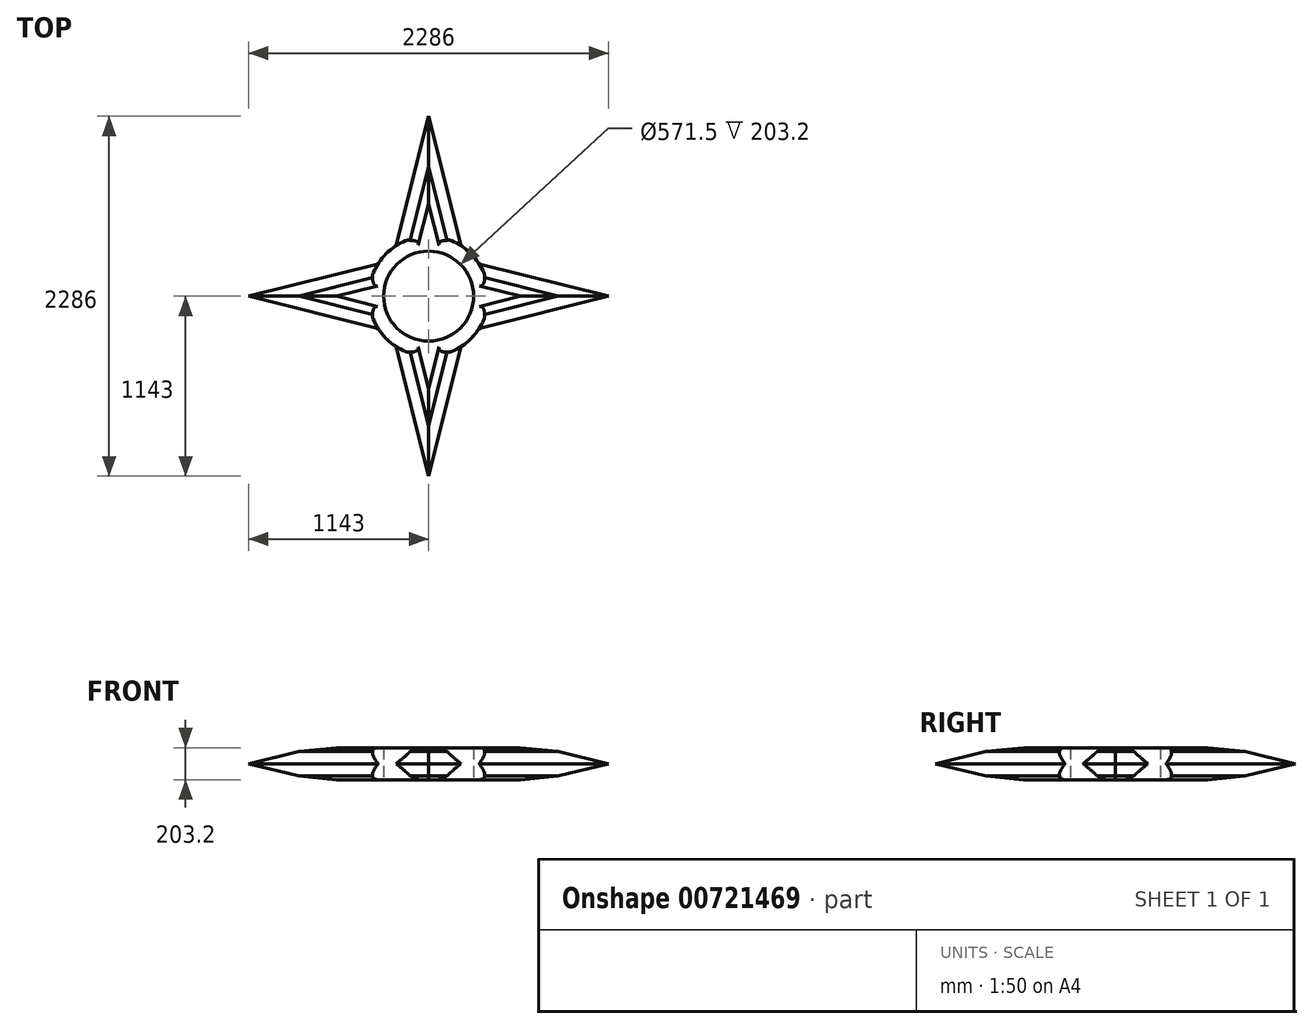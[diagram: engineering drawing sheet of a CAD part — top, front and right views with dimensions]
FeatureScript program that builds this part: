
annotation { "Feature Type Name" : "Feature", "Feature Type Description" : "" }
export const myFeature = defineFeature(function(context is Context, id is Id, definition is map)
    precondition{}
    {
        {
            var Q0;
            Q0=qCreatedBy(makeId("Top.planeOp"),FACE);
            var sketch = newSketch(context, id + "F0", { "sketchPlane" : qUnion([Q0])});
            skCircle(sketch, "E0", {"center": v(0, 0) * mm, "radius": 292.1 * mm});
            skCircle(sketch, "E1", {"center": v(0, 0) * mm, "radius": 381 * mm});
            skLineSegment(sketch, "E2.bottom", {"start": v(0, 0) * mm, "end": v(381, 0) * mm});
            skLineSegment(sketch, "E2.left", {"start": v(0, 0) * mm, "end": v(0, 381) * mm});
            skLineSegment(sketch, "E3.bottom", {"start": v(0, 0) * mm, "end": v(-381, 0) * mm});
            skLineSegment(sketch, "E3.left", {"start": v(0, 0) * mm, "end": v(0, -381) * mm});
            skLineSegment(sketch, "E4", {"start": v(0, 381) * mm, "end": v(0, 1143) * mm});
            skLineSegment(sketch, "E5", {"start": v(381, 0) * mm, "end": v(1143, 0) * mm});
            skLineSegment(sketch, "E6", {"start": v(0, -381) * mm, "end": v(0, -1143) * mm});
            skLineSegment(sketch, "E7", {"start": v(-381, 0) * mm, "end": v(-1143, 0) * mm});
            skLineSegment(sketch, "E8", {"start": v(-190.5, 381) * mm, "end": v(0, 1143) * mm});
            skLineSegment(sketch, "E9", {"start": v(190.5, 381) * mm, "end": v(0, 1143) * mm});
            skLineSegment(sketch, "E10", {"start": v(381, 190.5) * mm, "end": v(1143, 0) * mm});
            skLineSegment(sketch, "E11", {"start": v(1143, 0) * mm, "end": v(381, -190.5) * mm});
            skLineSegment(sketch, "E12", {"start": v(-190.5, -381) * mm, "end": v(0, -1143) * mm});
            skLineSegment(sketch, "E13", {"start": v(190.5, -381) * mm, "end": v(0, -1143) * mm});
            skLineSegment(sketch, "E14", {"start": v(-381, 190.5) * mm, "end": v(-1143, 0) * mm});
            skLineSegment(sketch, "E15", {"start": v(-381, -190.5) * mm, "end": v(-1143, 0) * mm});
            skLineSegment(sketch, "E16", {"start": v(-381, 190.5) * mm, "end": v(-320.8, 205.55) * mm});
            skLineSegment(sketch, "E17", {"start": v(-381, -190.5) * mm, "end": v(-320.8, -205.55) * mm});
            skLineSegment(sketch, "E18", {"start": v(-190.5, 381) * mm, "end": v(-205.55, 320.8) * mm});
            skLineSegment(sketch, "E19", {"start": v(190.5, 381) * mm, "end": v(205.55, 320.8) * mm});
            skLineSegment(sketch, "E20", {"start": v(381, 190.5) * mm, "end": v(320.8, 205.55) * mm});
            skLineSegment(sketch, "E21", {"start": v(381, -190.5) * mm, "end": v(320.8, -205.55) * mm});
            skLineSegment(sketch, "E22", {"start": v(190.5, -381) * mm, "end": v(205.55, -320.8) * mm});
            skLineSegment(sketch, "E23", {"start": v(-190.5, -381) * mm, "end": v(-205.55, -320.8) * mm});
            skCircle(sketch, "E24", {"center": v(0, 0) * mm, "radius": 285.75 * mm});
            skSolve(sketch);
        }
        {
            var Q0;
            {var subQ0=sQuery(id+"F0.wireOp",EDGE,"E4");Q0=makeQuery(id+"F0.imprint","IMPRINT",FACE,{"disambiguationData":[TD([[makeQuery(id+"F0.imprint","IMPRINT",EDGE,{"derivedFrom":subQ0}),1.0]])]});}
            var Q1;
            {var subQ0=sQuery(id+"F0.wireOp",EDGE,"E4");Q1=makeQuery(id+"F0.imprint","IMPRINT",FACE,{"disambiguationData":[TD([[makeQuery(id+"F0.imprint","IMPRINT",EDGE,{"derivedFrom":subQ0}),-1.0]])]});}
            var Q2;
            {var subQ0=sQuery(id+"F0.wireOp",EDGE,"E7");Q2=makeQuery(id+"F0.imprint","IMPRINT",FACE,{"disambiguationData":[TD([[makeQuery(id+"F0.imprint","IMPRINT",EDGE,{"derivedFrom":subQ0}),-1.0]])]});}
            var Q3;
            {var subQ0=sQuery(id+"F0.wireOp",EDGE,"E7");Q3=makeQuery(id+"F0.imprint","IMPRINT",FACE,{"disambiguationData":[TD([[makeQuery(id+"F0.imprint","IMPRINT",EDGE,{"derivedFrom":subQ0}),1.0]])]});}
            var Q4;
            {var subQ0=sQuery(id+"F0.wireOp",EDGE,"E6");Q4=makeQuery(id+"F0.imprint","IMPRINT",FACE,{"disambiguationData":[TD([[makeQuery(id+"F0.imprint","IMPRINT",EDGE,{"derivedFrom":subQ0}),-1.0]])]});}
            var Q5;
            {var subQ0=sQuery(id+"F0.wireOp",EDGE,"E6");Q5=makeQuery(id+"F0.imprint","IMPRINT",FACE,{"disambiguationData":[TD([[makeQuery(id+"F0.imprint","IMPRINT",EDGE,{"derivedFrom":subQ0}),1.0]])]});}
            var Q6;
            {var subQ0=sQuery(id+"F0.wireOp",EDGE,"E5");Q6=makeQuery(id+"F0.imprint","IMPRINT",FACE,{"disambiguationData":[TD([[makeQuery(id+"F0.imprint","IMPRINT",EDGE,{"derivedFrom":subQ0}),-1.0]])]});}
            var Q7;
            {var subQ0=sQuery(id+"F0.wireOp",EDGE,"E5");Q7=makeQuery(id+"F0.imprint","IMPRINT",FACE,{"disambiguationData":[TD([[makeQuery(id+"F0.imprint","IMPRINT",EDGE,{"derivedFrom":subQ0}),1.0]])]});}
            var Q8;
            {var subQ0=sQuery(id+"F0.wireOp",EDGE,"E2.left");var subQ6=sQuery(id+"F0.wireOp",EDGE,"E0");var subQ9=makeQuery(id+"F0.imprint","INTERSECT",VERTEX,{"derivedFrom":[subQ6,subQ0]});Q8=makeQuery(id+"F0.imprint","IMPRINT",FACE,{"disambiguationData":[TD([[makeQuery(id+"F0.imprint","IMPRINT",EDGE,{"disambiguationData":[TD([[subQ9,1.0]])],"derivedFrom":subQ6}),-1.0]])]});}
            var Q9;
            {var subQ5=sQuery(id+"F0.wireOp",EDGE,"E2.left");var subQ7=sQuery(id+"F0.wireOp",EDGE,"E0");var subQ8=makeQuery(id+"F0.imprint","INTERSECT",VERTEX,{"derivedFrom":[subQ7,subQ5]});Q9=makeQuery(id+"F0.imprint","IMPRINT",FACE,{"disambiguationData":[TD([[makeQuery(id+"F0.imprint","IMPRINT",EDGE,{"disambiguationData":[TD([[subQ8,-1.0]])],"derivedFrom":subQ7}),-1.0]])]});}
            var Q10;
            {var subQ0=sQuery(id+"F0.wireOp",EDGE,"E2.bottom");var subQ5=sQuery(id+"F0.wireOp",EDGE,"E0");var subQ6=makeQuery(id+"F0.imprint","INTERSECT",VERTEX,{"derivedFrom":[subQ5,subQ0]});Q10=makeQuery(id+"F0.imprint","IMPRINT",FACE,{"disambiguationData":[TD([[makeQuery(id+"F0.imprint","IMPRINT",EDGE,{"disambiguationData":[TD([[subQ6,1.0]])],"derivedFrom":subQ5}),-1.0]])]});}
            var Q11;
            {var subQ0=sQuery(id+"F0.wireOp",EDGE,"E3.bottom");var subQ1=sQuery(id+"F0.wireOp",EDGE,"E0");var subQ2=makeQuery(id+"F0.imprint","INTERSECT",VERTEX,{"derivedFrom":[subQ1,subQ0]});Q11=makeQuery(id+"F0.imprint","IMPRINT",FACE,{"disambiguationData":[TD([[makeQuery(id+"F0.imprint","IMPRINT",EDGE,{"disambiguationData":[TD([[subQ2,-1.0]])],"derivedFrom":subQ1}),1.0]])]});}
            var Q12;
            {var subQ0=sQuery(id+"F0.wireOp",EDGE,"E2.left");var subQ1=sQuery(id+"F0.wireOp",EDGE,"E0");var subQ2=makeQuery(id+"F0.imprint","INTERSECT",VERTEX,{"derivedFrom":[subQ1,subQ0]});Q12=makeQuery(id+"F0.imprint","IMPRINT",FACE,{"disambiguationData":[TD([[makeQuery(id+"F0.imprint","IMPRINT",EDGE,{"disambiguationData":[TD([[subQ2,-1.0]])],"derivedFrom":subQ1}),1.0]])]});}
            var Q13;
            {var subQ0=sQuery(id+"F0.wireOp",EDGE,"E2.bottom");var subQ1=sQuery(id+"F0.wireOp",EDGE,"E0");var subQ2=makeQuery(id+"F0.imprint","INTERSECT",VERTEX,{"derivedFrom":[subQ1,subQ0]});Q13=makeQuery(id+"F0.imprint","IMPRINT",FACE,{"disambiguationData":[TD([[makeQuery(id+"F0.imprint","IMPRINT",EDGE,{"disambiguationData":[TD([[subQ2,1.0]])],"derivedFrom":subQ1}),1.0]])]});}
            var Q14;
            {var subQ0=sQuery(id+"F0.wireOp",EDGE,"E2.left");var subQ1=sQuery(id+"F0.wireOp",EDGE,"E0");var subQ2=makeQuery(id+"F0.imprint","INTERSECT",VERTEX,{"derivedFrom":[subQ1,subQ0]});Q14=makeQuery(id+"F0.imprint","IMPRINT",FACE,{"disambiguationData":[TD([[makeQuery(id+"F0.imprint","IMPRINT",EDGE,{"disambiguationData":[TD([[subQ2,1.0]])],"derivedFrom":subQ1}),1.0]])]});}
            var Q15;
            {var subQ3=sQuery(id+"F0.wireOp",EDGE,"E3.bottom");var subQ7=sQuery(id+"F0.wireOp",EDGE,"E0");var subQ8=makeQuery(id+"F0.imprint","INTERSECT",VERTEX,{"derivedFrom":[subQ7,subQ3]});Q15=makeQuery(id+"F0.imprint","IMPRINT",FACE,{"disambiguationData":[TD([[makeQuery(id+"F0.imprint","IMPRINT",EDGE,{"disambiguationData":[TD([[subQ8,-1.0]])],"derivedFrom":subQ7}),-1.0]])]});}
            extrude(context, id + "F1", {"entities" : qUnion([Q0, Q1, Q2, Q3, Q4, Q5, Q6, Q7, Q8, Q9, Q10, Q11, Q12, Q13, Q14, Q15]), "depth" : 203.2 * mm, "offsetDistance" : 25.4 * mm});
        }
        {
            var Q0;
            Q0=makeQuery(id+"F1.opExtrude","CAP_EDGE",EDGE,{"disambiguationData":[OSD([sQuery(id+"F0.wireOp",EDGE,"E15"),sQuery(id+"F0.wireOp",EDGE,"E17")])],"isStart":false});
            var Q1;
            Q1=makeQuery(id+"F1.opExtrude","CAP_EDGE",EDGE,{"disambiguationData":[OSD([sQuery(id+"F0.wireOp",EDGE,"E15"),sQuery(id+"F0.wireOp",EDGE,"E17")])],"isStart":true});
            var Q2;
            Q2=makeQuery(id+"F1.opExtrude","CAP_EDGE",EDGE,{"disambiguationData":[OSD([sQuery(id+"F0.wireOp",EDGE,"E14"),sQuery(id+"F0.wireOp",EDGE,"E16")])],"isStart":false});
            var Q3;
            Q3=makeQuery(id+"F1.opExtrude","CAP_EDGE",EDGE,{"disambiguationData":[OSD([sQuery(id+"F0.wireOp",EDGE,"E14"),sQuery(id+"F0.wireOp",EDGE,"E16")])],"isStart":true});
            var Q4;
            Q4=makeQuery(id+"F1.opExtrude","CAP_EDGE",EDGE,{"disambiguationData":[OSD([sQuery(id+"F0.wireOp",EDGE,"E8"),sQuery(id+"F0.wireOp",EDGE,"E18")])],"isStart":false});
            var Q5;
            Q5=makeQuery(id+"F1.opExtrude","CAP_EDGE",EDGE,{"disambiguationData":[OSD([sQuery(id+"F0.wireOp",EDGE,"E8"),sQuery(id+"F0.wireOp",EDGE,"E18")])],"isStart":true});
            var Q6;
            Q6=makeQuery(id+"F1.opExtrude","CAP_EDGE",EDGE,{"disambiguationData":[OSD([sQuery(id+"F0.wireOp",EDGE,"E9"),sQuery(id+"F0.wireOp",EDGE,"E19")])],"isStart":false});
            var Q7;
            Q7=makeQuery(id+"F1.opExtrude","CAP_EDGE",EDGE,{"disambiguationData":[OSD([sQuery(id+"F0.wireOp",EDGE,"E9"),sQuery(id+"F0.wireOp",EDGE,"E19")])],"isStart":true});
            var Q8;
            Q8=makeQuery(id+"F1.opExtrude","CAP_EDGE",EDGE,{"disambiguationData":[OSD([sQuery(id+"F0.wireOp",EDGE,"E10"),sQuery(id+"F0.wireOp",EDGE,"E20")])],"isStart":false});
            var Q9;
            Q9=makeQuery(id+"F1.opExtrude","CAP_EDGE",EDGE,{"disambiguationData":[OSD([sQuery(id+"F0.wireOp",EDGE,"E10"),sQuery(id+"F0.wireOp",EDGE,"E20")])],"isStart":true});
            var Q10;
            Q10=makeQuery(id+"F1.opExtrude","CAP_EDGE",EDGE,{"disambiguationData":[OSD([sQuery(id+"F0.wireOp",EDGE,"E11"),sQuery(id+"F0.wireOp",EDGE,"E21")])],"isStart":false});
            var Q11;
            Q11=makeQuery(id+"F1.opExtrude","CAP_EDGE",EDGE,{"disambiguationData":[OSD([sQuery(id+"F0.wireOp",EDGE,"E11"),sQuery(id+"F0.wireOp",EDGE,"E21")])],"isStart":true});
            var Q12;
            Q12=makeQuery(id+"F1.opExtrude","CAP_EDGE",EDGE,{"disambiguationData":[OSD([sQuery(id+"F0.wireOp",EDGE,"E13"),sQuery(id+"F0.wireOp",EDGE,"E22")])],"isStart":false});
            var Q13;
            Q13=makeQuery(id+"F1.opExtrude","CAP_EDGE",EDGE,{"disambiguationData":[OSD([sQuery(id+"F0.wireOp",EDGE,"E13"),sQuery(id+"F0.wireOp",EDGE,"E22")])],"isStart":true});
            var Q14;
            Q14=makeQuery(id+"F1.opExtrude","CAP_EDGE",EDGE,{"disambiguationData":[OSD([sQuery(id+"F0.wireOp",EDGE,"E12"),sQuery(id+"F0.wireOp",EDGE,"E23")])],"isStart":false});
            var Q15;
            Q15=makeQuery(id+"F1.opExtrude","CAP_EDGE",EDGE,{"disambiguationData":[OSD([sQuery(id+"F0.wireOp",EDGE,"E12"),sQuery(id+"F0.wireOp",EDGE,"E23")])],"isStart":true});
            chamfer(context, id + "F2", {"entities" : qUnion([Q0, Q1, Q2, Q3, Q4, Q5, Q6, Q7, Q8, Q9, Q10, Q11, Q12, Q13, Q14, Q15]), "width" : 101.6 * mm, "tangentPropagation" : true});
        }
        {
            var Q0;
            {var subQ0=sQuery(id+"F0.wireOp",EDGE,"E23");var subQ1=sQuery(id+"F0.wireOp",EDGE,"E12");Q0=makeQuery(id+"F2.opChamfer","BLEND_EDGE",EDGE,{"blendedFrom":[makeQuery(id+"F1.opExtrude","CAP_EDGE",EDGE,{"disambiguationData":[OSD([subQ1,subQ0])],"isStart":false}),makeQuery(id+"F1.opExtrude","CAP_FACE",FACE,{"disambiguationData":[OSD([sQuery(id+"F0.wireOp",EDGE,"E0"),sQuery(id+"F0.wireOp",EDGE,"E1"),sQuery(id+"F0.wireOp",EDGE,"E8"),sQuery(id+"F0.wireOp",EDGE,"E9"),sQuery(id+"F0.wireOp",EDGE,"E10"),sQuery(id+"F0.wireOp",EDGE,"E11"),subQ1,sQuery(id+"F0.wireOp",EDGE,"E13"),sQuery(id+"F0.wireOp",EDGE,"E14"),sQuery(id+"F0.wireOp",EDGE,"E15"),sQuery(id+"F0.wireOp",EDGE,"E16"),sQuery(id+"F0.wireOp",EDGE,"E17"),sQuery(id+"F0.wireOp",EDGE,"E18"),sQuery(id+"F0.wireOp",EDGE,"E19"),sQuery(id+"F0.wireOp",EDGE,"E20"),sQuery(id+"F0.wireOp",EDGE,"E21"),sQuery(id+"F0.wireOp",EDGE,"E22"),subQ0])],"isStart":false})],"blendedInto":[makeQuery(id+"F1.opExtrude","CAP_FACE",FACE,{"disambiguationData":[OSD([sQuery(id+"F0.wireOp",EDGE,"E0"),sQuery(id+"F0.wireOp",EDGE,"E1"),sQuery(id+"F0.wireOp",EDGE,"E8"),sQuery(id+"F0.wireOp",EDGE,"E9"),sQuery(id+"F0.wireOp",EDGE,"E10"),sQuery(id+"F0.wireOp",EDGE,"E11"),subQ1,sQuery(id+"F0.wireOp",EDGE,"E13"),sQuery(id+"F0.wireOp",EDGE,"E14"),sQuery(id+"F0.wireOp",EDGE,"E15"),sQuery(id+"F0.wireOp",EDGE,"E16"),sQuery(id+"F0.wireOp",EDGE,"E17"),sQuery(id+"F0.wireOp",EDGE,"E18"),sQuery(id+"F0.wireOp",EDGE,"E19"),sQuery(id+"F0.wireOp",EDGE,"E20"),sQuery(id+"F0.wireOp",EDGE,"E21"),sQuery(id+"F0.wireOp",EDGE,"E22"),subQ0])],"isStart":false})]});}
            var Q1;
            {var subQ0=sQuery(id+"F0.wireOp",EDGE,"E22");var subQ1=sQuery(id+"F0.wireOp",EDGE,"E13");Q1=makeQuery(id+"F2.opChamfer","BLEND_EDGE",EDGE,{"blendedFrom":[makeQuery(id+"F1.opExtrude","CAP_EDGE",EDGE,{"disambiguationData":[OSD([subQ1,subQ0])],"isStart":false}),makeQuery(id+"F1.opExtrude","CAP_FACE",FACE,{"disambiguationData":[OSD([sQuery(id+"F0.wireOp",EDGE,"E0"),sQuery(id+"F0.wireOp",EDGE,"E1"),sQuery(id+"F0.wireOp",EDGE,"E8"),sQuery(id+"F0.wireOp",EDGE,"E9"),sQuery(id+"F0.wireOp",EDGE,"E10"),sQuery(id+"F0.wireOp",EDGE,"E11"),sQuery(id+"F0.wireOp",EDGE,"E12"),subQ1,sQuery(id+"F0.wireOp",EDGE,"E14"),sQuery(id+"F0.wireOp",EDGE,"E15"),sQuery(id+"F0.wireOp",EDGE,"E16"),sQuery(id+"F0.wireOp",EDGE,"E17"),sQuery(id+"F0.wireOp",EDGE,"E18"),sQuery(id+"F0.wireOp",EDGE,"E19"),sQuery(id+"F0.wireOp",EDGE,"E20"),sQuery(id+"F0.wireOp",EDGE,"E21"),subQ0,sQuery(id+"F0.wireOp",EDGE,"E23")])],"isStart":false})],"blendedInto":[makeQuery(id+"F1.opExtrude","CAP_FACE",FACE,{"disambiguationData":[OSD([sQuery(id+"F0.wireOp",EDGE,"E0"),sQuery(id+"F0.wireOp",EDGE,"E1"),sQuery(id+"F0.wireOp",EDGE,"E8"),sQuery(id+"F0.wireOp",EDGE,"E9"),sQuery(id+"F0.wireOp",EDGE,"E10"),sQuery(id+"F0.wireOp",EDGE,"E11"),sQuery(id+"F0.wireOp",EDGE,"E12"),subQ1,sQuery(id+"F0.wireOp",EDGE,"E14"),sQuery(id+"F0.wireOp",EDGE,"E15"),sQuery(id+"F0.wireOp",EDGE,"E16"),sQuery(id+"F0.wireOp",EDGE,"E17"),sQuery(id+"F0.wireOp",EDGE,"E18"),sQuery(id+"F0.wireOp",EDGE,"E19"),sQuery(id+"F0.wireOp",EDGE,"E20"),sQuery(id+"F0.wireOp",EDGE,"E21"),subQ0,sQuery(id+"F0.wireOp",EDGE,"E23")])],"isStart":false})]});}
            var Q2;
            {var subQ0=sQuery(id+"F0.wireOp",EDGE,"E21");var subQ1=sQuery(id+"F0.wireOp",EDGE,"E11");Q2=makeQuery(id+"F2.opChamfer","BLEND_EDGE",EDGE,{"blendedFrom":[makeQuery(id+"F1.opExtrude","CAP_EDGE",EDGE,{"disambiguationData":[OSD([subQ1,subQ0])],"isStart":false}),makeQuery(id+"F1.opExtrude","CAP_FACE",FACE,{"disambiguationData":[OSD([sQuery(id+"F0.wireOp",EDGE,"E0"),sQuery(id+"F0.wireOp",EDGE,"E1"),sQuery(id+"F0.wireOp",EDGE,"E8"),sQuery(id+"F0.wireOp",EDGE,"E9"),sQuery(id+"F0.wireOp",EDGE,"E10"),subQ1,sQuery(id+"F0.wireOp",EDGE,"E12"),sQuery(id+"F0.wireOp",EDGE,"E13"),sQuery(id+"F0.wireOp",EDGE,"E14"),sQuery(id+"F0.wireOp",EDGE,"E15"),sQuery(id+"F0.wireOp",EDGE,"E16"),sQuery(id+"F0.wireOp",EDGE,"E17"),sQuery(id+"F0.wireOp",EDGE,"E18"),sQuery(id+"F0.wireOp",EDGE,"E19"),sQuery(id+"F0.wireOp",EDGE,"E20"),subQ0,sQuery(id+"F0.wireOp",EDGE,"E22"),sQuery(id+"F0.wireOp",EDGE,"E23")])],"isStart":false})],"blendedInto":[makeQuery(id+"F1.opExtrude","CAP_FACE",FACE,{"disambiguationData":[OSD([sQuery(id+"F0.wireOp",EDGE,"E0"),sQuery(id+"F0.wireOp",EDGE,"E1"),sQuery(id+"F0.wireOp",EDGE,"E8"),sQuery(id+"F0.wireOp",EDGE,"E9"),sQuery(id+"F0.wireOp",EDGE,"E10"),subQ1,sQuery(id+"F0.wireOp",EDGE,"E12"),sQuery(id+"F0.wireOp",EDGE,"E13"),sQuery(id+"F0.wireOp",EDGE,"E14"),sQuery(id+"F0.wireOp",EDGE,"E15"),sQuery(id+"F0.wireOp",EDGE,"E16"),sQuery(id+"F0.wireOp",EDGE,"E17"),sQuery(id+"F0.wireOp",EDGE,"E18"),sQuery(id+"F0.wireOp",EDGE,"E19"),sQuery(id+"F0.wireOp",EDGE,"E20"),subQ0,sQuery(id+"F0.wireOp",EDGE,"E22"),sQuery(id+"F0.wireOp",EDGE,"E23")])],"isStart":false})]});}
            var Q3;
            {var subQ0=sQuery(id+"F0.wireOp",EDGE,"E20");var subQ1=sQuery(id+"F0.wireOp",EDGE,"E10");Q3=makeQuery(id+"F2.opChamfer","BLEND_EDGE",EDGE,{"blendedFrom":[makeQuery(id+"F1.opExtrude","CAP_EDGE",EDGE,{"disambiguationData":[OSD([subQ1,subQ0])],"isStart":false}),makeQuery(id+"F1.opExtrude","CAP_FACE",FACE,{"disambiguationData":[OSD([sQuery(id+"F0.wireOp",EDGE,"E0"),sQuery(id+"F0.wireOp",EDGE,"E1"),sQuery(id+"F0.wireOp",EDGE,"E8"),sQuery(id+"F0.wireOp",EDGE,"E9"),subQ1,sQuery(id+"F0.wireOp",EDGE,"E11"),sQuery(id+"F0.wireOp",EDGE,"E12"),sQuery(id+"F0.wireOp",EDGE,"E13"),sQuery(id+"F0.wireOp",EDGE,"E14"),sQuery(id+"F0.wireOp",EDGE,"E15"),sQuery(id+"F0.wireOp",EDGE,"E16"),sQuery(id+"F0.wireOp",EDGE,"E17"),sQuery(id+"F0.wireOp",EDGE,"E18"),sQuery(id+"F0.wireOp",EDGE,"E19"),subQ0,sQuery(id+"F0.wireOp",EDGE,"E21"),sQuery(id+"F0.wireOp",EDGE,"E22"),sQuery(id+"F0.wireOp",EDGE,"E23")])],"isStart":false})],"blendedInto":[makeQuery(id+"F1.opExtrude","CAP_FACE",FACE,{"disambiguationData":[OSD([sQuery(id+"F0.wireOp",EDGE,"E0"),sQuery(id+"F0.wireOp",EDGE,"E1"),sQuery(id+"F0.wireOp",EDGE,"E8"),sQuery(id+"F0.wireOp",EDGE,"E9"),subQ1,sQuery(id+"F0.wireOp",EDGE,"E11"),sQuery(id+"F0.wireOp",EDGE,"E12"),sQuery(id+"F0.wireOp",EDGE,"E13"),sQuery(id+"F0.wireOp",EDGE,"E14"),sQuery(id+"F0.wireOp",EDGE,"E15"),sQuery(id+"F0.wireOp",EDGE,"E16"),sQuery(id+"F0.wireOp",EDGE,"E17"),sQuery(id+"F0.wireOp",EDGE,"E18"),sQuery(id+"F0.wireOp",EDGE,"E19"),subQ0,sQuery(id+"F0.wireOp",EDGE,"E21"),sQuery(id+"F0.wireOp",EDGE,"E22"),sQuery(id+"F0.wireOp",EDGE,"E23")])],"isStart":false})]});}
            var Q4;
            {var subQ0=sQuery(id+"F0.wireOp",EDGE,"E19");var subQ1=sQuery(id+"F0.wireOp",EDGE,"E9");Q4=makeQuery(id+"F2.opChamfer","BLEND_EDGE",EDGE,{"blendedFrom":[makeQuery(id+"F1.opExtrude","CAP_EDGE",EDGE,{"disambiguationData":[OSD([subQ1,subQ0])],"isStart":false}),makeQuery(id+"F1.opExtrude","CAP_FACE",FACE,{"disambiguationData":[OSD([sQuery(id+"F0.wireOp",EDGE,"E0"),sQuery(id+"F0.wireOp",EDGE,"E1"),sQuery(id+"F0.wireOp",EDGE,"E8"),subQ1,sQuery(id+"F0.wireOp",EDGE,"E10"),sQuery(id+"F0.wireOp",EDGE,"E11"),sQuery(id+"F0.wireOp",EDGE,"E12"),sQuery(id+"F0.wireOp",EDGE,"E13"),sQuery(id+"F0.wireOp",EDGE,"E14"),sQuery(id+"F0.wireOp",EDGE,"E15"),sQuery(id+"F0.wireOp",EDGE,"E16"),sQuery(id+"F0.wireOp",EDGE,"E17"),sQuery(id+"F0.wireOp",EDGE,"E18"),subQ0,sQuery(id+"F0.wireOp",EDGE,"E20"),sQuery(id+"F0.wireOp",EDGE,"E21"),sQuery(id+"F0.wireOp",EDGE,"E22"),sQuery(id+"F0.wireOp",EDGE,"E23")])],"isStart":false})],"blendedInto":[makeQuery(id+"F1.opExtrude","CAP_FACE",FACE,{"disambiguationData":[OSD([sQuery(id+"F0.wireOp",EDGE,"E0"),sQuery(id+"F0.wireOp",EDGE,"E1"),sQuery(id+"F0.wireOp",EDGE,"E8"),subQ1,sQuery(id+"F0.wireOp",EDGE,"E10"),sQuery(id+"F0.wireOp",EDGE,"E11"),sQuery(id+"F0.wireOp",EDGE,"E12"),sQuery(id+"F0.wireOp",EDGE,"E13"),sQuery(id+"F0.wireOp",EDGE,"E14"),sQuery(id+"F0.wireOp",EDGE,"E15"),sQuery(id+"F0.wireOp",EDGE,"E16"),sQuery(id+"F0.wireOp",EDGE,"E17"),sQuery(id+"F0.wireOp",EDGE,"E18"),subQ0,sQuery(id+"F0.wireOp",EDGE,"E20"),sQuery(id+"F0.wireOp",EDGE,"E21"),sQuery(id+"F0.wireOp",EDGE,"E22"),sQuery(id+"F0.wireOp",EDGE,"E23")])],"isStart":false})]});}
            var Q5;
            {var subQ0=sQuery(id+"F0.wireOp",EDGE,"E18");var subQ1=sQuery(id+"F0.wireOp",EDGE,"E8");Q5=makeQuery(id+"F2.opChamfer","BLEND_EDGE",EDGE,{"blendedFrom":[makeQuery(id+"F1.opExtrude","CAP_EDGE",EDGE,{"disambiguationData":[OSD([subQ1,subQ0])],"isStart":false}),makeQuery(id+"F1.opExtrude","CAP_FACE",FACE,{"disambiguationData":[OSD([sQuery(id+"F0.wireOp",EDGE,"E0"),sQuery(id+"F0.wireOp",EDGE,"E1"),subQ1,sQuery(id+"F0.wireOp",EDGE,"E9"),sQuery(id+"F0.wireOp",EDGE,"E10"),sQuery(id+"F0.wireOp",EDGE,"E11"),sQuery(id+"F0.wireOp",EDGE,"E12"),sQuery(id+"F0.wireOp",EDGE,"E13"),sQuery(id+"F0.wireOp",EDGE,"E14"),sQuery(id+"F0.wireOp",EDGE,"E15"),sQuery(id+"F0.wireOp",EDGE,"E16"),sQuery(id+"F0.wireOp",EDGE,"E17"),subQ0,sQuery(id+"F0.wireOp",EDGE,"E19"),sQuery(id+"F0.wireOp",EDGE,"E20"),sQuery(id+"F0.wireOp",EDGE,"E21"),sQuery(id+"F0.wireOp",EDGE,"E22"),sQuery(id+"F0.wireOp",EDGE,"E23")])],"isStart":false})],"blendedInto":[makeQuery(id+"F1.opExtrude","CAP_FACE",FACE,{"disambiguationData":[OSD([sQuery(id+"F0.wireOp",EDGE,"E0"),sQuery(id+"F0.wireOp",EDGE,"E1"),subQ1,sQuery(id+"F0.wireOp",EDGE,"E9"),sQuery(id+"F0.wireOp",EDGE,"E10"),sQuery(id+"F0.wireOp",EDGE,"E11"),sQuery(id+"F0.wireOp",EDGE,"E12"),sQuery(id+"F0.wireOp",EDGE,"E13"),sQuery(id+"F0.wireOp",EDGE,"E14"),sQuery(id+"F0.wireOp",EDGE,"E15"),sQuery(id+"F0.wireOp",EDGE,"E16"),sQuery(id+"F0.wireOp",EDGE,"E17"),subQ0,sQuery(id+"F0.wireOp",EDGE,"E19"),sQuery(id+"F0.wireOp",EDGE,"E20"),sQuery(id+"F0.wireOp",EDGE,"E21"),sQuery(id+"F0.wireOp",EDGE,"E22"),sQuery(id+"F0.wireOp",EDGE,"E23")])],"isStart":false})]});}
            var Q6;
            {var subQ0=sQuery(id+"F0.wireOp",EDGE,"E16");var subQ1=sQuery(id+"F0.wireOp",EDGE,"E14");Q6=makeQuery(id+"F2.opChamfer","BLEND_EDGE",EDGE,{"blendedFrom":[makeQuery(id+"F1.opExtrude","CAP_EDGE",EDGE,{"disambiguationData":[OSD([subQ1,subQ0])],"isStart":false}),makeQuery(id+"F1.opExtrude","CAP_FACE",FACE,{"disambiguationData":[OSD([sQuery(id+"F0.wireOp",EDGE,"E0"),sQuery(id+"F0.wireOp",EDGE,"E1"),sQuery(id+"F0.wireOp",EDGE,"E8"),sQuery(id+"F0.wireOp",EDGE,"E9"),sQuery(id+"F0.wireOp",EDGE,"E10"),sQuery(id+"F0.wireOp",EDGE,"E11"),sQuery(id+"F0.wireOp",EDGE,"E12"),sQuery(id+"F0.wireOp",EDGE,"E13"),subQ1,sQuery(id+"F0.wireOp",EDGE,"E15"),subQ0,sQuery(id+"F0.wireOp",EDGE,"E17"),sQuery(id+"F0.wireOp",EDGE,"E18"),sQuery(id+"F0.wireOp",EDGE,"E19"),sQuery(id+"F0.wireOp",EDGE,"E20"),sQuery(id+"F0.wireOp",EDGE,"E21"),sQuery(id+"F0.wireOp",EDGE,"E22"),sQuery(id+"F0.wireOp",EDGE,"E23")])],"isStart":false})],"blendedInto":[makeQuery(id+"F1.opExtrude","CAP_FACE",FACE,{"disambiguationData":[OSD([sQuery(id+"F0.wireOp",EDGE,"E0"),sQuery(id+"F0.wireOp",EDGE,"E1"),sQuery(id+"F0.wireOp",EDGE,"E8"),sQuery(id+"F0.wireOp",EDGE,"E9"),sQuery(id+"F0.wireOp",EDGE,"E10"),sQuery(id+"F0.wireOp",EDGE,"E11"),sQuery(id+"F0.wireOp",EDGE,"E12"),sQuery(id+"F0.wireOp",EDGE,"E13"),subQ1,sQuery(id+"F0.wireOp",EDGE,"E15"),subQ0,sQuery(id+"F0.wireOp",EDGE,"E17"),sQuery(id+"F0.wireOp",EDGE,"E18"),sQuery(id+"F0.wireOp",EDGE,"E19"),sQuery(id+"F0.wireOp",EDGE,"E20"),sQuery(id+"F0.wireOp",EDGE,"E21"),sQuery(id+"F0.wireOp",EDGE,"E22"),sQuery(id+"F0.wireOp",EDGE,"E23")])],"isStart":false})]});}
            var Q7;
            {var subQ0=sQuery(id+"F0.wireOp",EDGE,"E17");var subQ1=sQuery(id+"F0.wireOp",EDGE,"E15");Q7=makeQuery(id+"F2.opChamfer","BLEND_EDGE",EDGE,{"blendedFrom":[makeQuery(id+"F1.opExtrude","CAP_EDGE",EDGE,{"disambiguationData":[OSD([subQ1,subQ0])],"isStart":false}),makeQuery(id+"F1.opExtrude","CAP_FACE",FACE,{"disambiguationData":[OSD([sQuery(id+"F0.wireOp",EDGE,"E0"),sQuery(id+"F0.wireOp",EDGE,"E1"),sQuery(id+"F0.wireOp",EDGE,"E8"),sQuery(id+"F0.wireOp",EDGE,"E9"),sQuery(id+"F0.wireOp",EDGE,"E10"),sQuery(id+"F0.wireOp",EDGE,"E11"),sQuery(id+"F0.wireOp",EDGE,"E12"),sQuery(id+"F0.wireOp",EDGE,"E13"),sQuery(id+"F0.wireOp",EDGE,"E14"),subQ1,sQuery(id+"F0.wireOp",EDGE,"E16"),subQ0,sQuery(id+"F0.wireOp",EDGE,"E18"),sQuery(id+"F0.wireOp",EDGE,"E19"),sQuery(id+"F0.wireOp",EDGE,"E20"),sQuery(id+"F0.wireOp",EDGE,"E21"),sQuery(id+"F0.wireOp",EDGE,"E22"),sQuery(id+"F0.wireOp",EDGE,"E23")])],"isStart":false})],"blendedInto":[makeQuery(id+"F1.opExtrude","CAP_FACE",FACE,{"disambiguationData":[OSD([sQuery(id+"F0.wireOp",EDGE,"E0"),sQuery(id+"F0.wireOp",EDGE,"E1"),sQuery(id+"F0.wireOp",EDGE,"E8"),sQuery(id+"F0.wireOp",EDGE,"E9"),sQuery(id+"F0.wireOp",EDGE,"E10"),sQuery(id+"F0.wireOp",EDGE,"E11"),sQuery(id+"F0.wireOp",EDGE,"E12"),sQuery(id+"F0.wireOp",EDGE,"E13"),sQuery(id+"F0.wireOp",EDGE,"E14"),subQ1,sQuery(id+"F0.wireOp",EDGE,"E16"),subQ0,sQuery(id+"F0.wireOp",EDGE,"E18"),sQuery(id+"F0.wireOp",EDGE,"E19"),sQuery(id+"F0.wireOp",EDGE,"E20"),sQuery(id+"F0.wireOp",EDGE,"E21"),sQuery(id+"F0.wireOp",EDGE,"E22"),sQuery(id+"F0.wireOp",EDGE,"E23")])],"isStart":false})]});}
            var Q8;
            {var subQ0=sQuery(id+"F0.wireOp",EDGE,"E18");var subQ1=sQuery(id+"F0.wireOp",EDGE,"E8");Q8=makeQuery(id+"F2.opChamfer","BLEND_EDGE",EDGE,{"blendedFrom":[makeQuery(id+"F1.opExtrude","CAP_EDGE",EDGE,{"disambiguationData":[OSD([subQ1,subQ0])],"isStart":true}),makeQuery(id+"F1.opExtrude","CAP_FACE",FACE,{"disambiguationData":[OSD([sQuery(id+"F0.wireOp",EDGE,"E0"),sQuery(id+"F0.wireOp",EDGE,"E1"),subQ1,sQuery(id+"F0.wireOp",EDGE,"E9"),sQuery(id+"F0.wireOp",EDGE,"E10"),sQuery(id+"F0.wireOp",EDGE,"E11"),sQuery(id+"F0.wireOp",EDGE,"E12"),sQuery(id+"F0.wireOp",EDGE,"E13"),sQuery(id+"F0.wireOp",EDGE,"E14"),sQuery(id+"F0.wireOp",EDGE,"E15"),sQuery(id+"F0.wireOp",EDGE,"E16"),sQuery(id+"F0.wireOp",EDGE,"E17"),subQ0,sQuery(id+"F0.wireOp",EDGE,"E19"),sQuery(id+"F0.wireOp",EDGE,"E20"),sQuery(id+"F0.wireOp",EDGE,"E21"),sQuery(id+"F0.wireOp",EDGE,"E22"),sQuery(id+"F0.wireOp",EDGE,"E23")])],"isStart":true})],"blendedInto":[makeQuery(id+"F1.opExtrude","CAP_FACE",FACE,{"disambiguationData":[OSD([sQuery(id+"F0.wireOp",EDGE,"E0"),sQuery(id+"F0.wireOp",EDGE,"E1"),subQ1,sQuery(id+"F0.wireOp",EDGE,"E9"),sQuery(id+"F0.wireOp",EDGE,"E10"),sQuery(id+"F0.wireOp",EDGE,"E11"),sQuery(id+"F0.wireOp",EDGE,"E12"),sQuery(id+"F0.wireOp",EDGE,"E13"),sQuery(id+"F0.wireOp",EDGE,"E14"),sQuery(id+"F0.wireOp",EDGE,"E15"),sQuery(id+"F0.wireOp",EDGE,"E16"),sQuery(id+"F0.wireOp",EDGE,"E17"),subQ0,sQuery(id+"F0.wireOp",EDGE,"E19"),sQuery(id+"F0.wireOp",EDGE,"E20"),sQuery(id+"F0.wireOp",EDGE,"E21"),sQuery(id+"F0.wireOp",EDGE,"E22"),sQuery(id+"F0.wireOp",EDGE,"E23")])],"isStart":true})]});}
            var Q9;
            {var subQ0=sQuery(id+"F0.wireOp",EDGE,"E19");var subQ1=sQuery(id+"F0.wireOp",EDGE,"E9");Q9=makeQuery(id+"F2.opChamfer","BLEND_EDGE",EDGE,{"blendedFrom":[makeQuery(id+"F1.opExtrude","CAP_EDGE",EDGE,{"disambiguationData":[OSD([subQ1,subQ0])],"isStart":true}),makeQuery(id+"F1.opExtrude","CAP_FACE",FACE,{"disambiguationData":[OSD([sQuery(id+"F0.wireOp",EDGE,"E0"),sQuery(id+"F0.wireOp",EDGE,"E1"),sQuery(id+"F0.wireOp",EDGE,"E8"),subQ1,sQuery(id+"F0.wireOp",EDGE,"E10"),sQuery(id+"F0.wireOp",EDGE,"E11"),sQuery(id+"F0.wireOp",EDGE,"E12"),sQuery(id+"F0.wireOp",EDGE,"E13"),sQuery(id+"F0.wireOp",EDGE,"E14"),sQuery(id+"F0.wireOp",EDGE,"E15"),sQuery(id+"F0.wireOp",EDGE,"E16"),sQuery(id+"F0.wireOp",EDGE,"E17"),sQuery(id+"F0.wireOp",EDGE,"E18"),subQ0,sQuery(id+"F0.wireOp",EDGE,"E20"),sQuery(id+"F0.wireOp",EDGE,"E21"),sQuery(id+"F0.wireOp",EDGE,"E22"),sQuery(id+"F0.wireOp",EDGE,"E23")])],"isStart":true})],"blendedInto":[makeQuery(id+"F1.opExtrude","CAP_FACE",FACE,{"disambiguationData":[OSD([sQuery(id+"F0.wireOp",EDGE,"E0"),sQuery(id+"F0.wireOp",EDGE,"E1"),sQuery(id+"F0.wireOp",EDGE,"E8"),subQ1,sQuery(id+"F0.wireOp",EDGE,"E10"),sQuery(id+"F0.wireOp",EDGE,"E11"),sQuery(id+"F0.wireOp",EDGE,"E12"),sQuery(id+"F0.wireOp",EDGE,"E13"),sQuery(id+"F0.wireOp",EDGE,"E14"),sQuery(id+"F0.wireOp",EDGE,"E15"),sQuery(id+"F0.wireOp",EDGE,"E16"),sQuery(id+"F0.wireOp",EDGE,"E17"),sQuery(id+"F0.wireOp",EDGE,"E18"),subQ0,sQuery(id+"F0.wireOp",EDGE,"E20"),sQuery(id+"F0.wireOp",EDGE,"E21"),sQuery(id+"F0.wireOp",EDGE,"E22"),sQuery(id+"F0.wireOp",EDGE,"E23")])],"isStart":true})]});}
            var Q10;
            {var subQ0=sQuery(id+"F0.wireOp",EDGE,"E20");var subQ1=sQuery(id+"F0.wireOp",EDGE,"E10");Q10=makeQuery(id+"F2.opChamfer","BLEND_EDGE",EDGE,{"blendedFrom":[makeQuery(id+"F1.opExtrude","CAP_EDGE",EDGE,{"disambiguationData":[OSD([subQ1,subQ0])],"isStart":true}),makeQuery(id+"F1.opExtrude","CAP_FACE",FACE,{"disambiguationData":[OSD([sQuery(id+"F0.wireOp",EDGE,"E0"),sQuery(id+"F0.wireOp",EDGE,"E1"),sQuery(id+"F0.wireOp",EDGE,"E8"),sQuery(id+"F0.wireOp",EDGE,"E9"),subQ1,sQuery(id+"F0.wireOp",EDGE,"E11"),sQuery(id+"F0.wireOp",EDGE,"E12"),sQuery(id+"F0.wireOp",EDGE,"E13"),sQuery(id+"F0.wireOp",EDGE,"E14"),sQuery(id+"F0.wireOp",EDGE,"E15"),sQuery(id+"F0.wireOp",EDGE,"E16"),sQuery(id+"F0.wireOp",EDGE,"E17"),sQuery(id+"F0.wireOp",EDGE,"E18"),sQuery(id+"F0.wireOp",EDGE,"E19"),subQ0,sQuery(id+"F0.wireOp",EDGE,"E21"),sQuery(id+"F0.wireOp",EDGE,"E22"),sQuery(id+"F0.wireOp",EDGE,"E23")])],"isStart":true})],"blendedInto":[makeQuery(id+"F1.opExtrude","CAP_FACE",FACE,{"disambiguationData":[OSD([sQuery(id+"F0.wireOp",EDGE,"E0"),sQuery(id+"F0.wireOp",EDGE,"E1"),sQuery(id+"F0.wireOp",EDGE,"E8"),sQuery(id+"F0.wireOp",EDGE,"E9"),subQ1,sQuery(id+"F0.wireOp",EDGE,"E11"),sQuery(id+"F0.wireOp",EDGE,"E12"),sQuery(id+"F0.wireOp",EDGE,"E13"),sQuery(id+"F0.wireOp",EDGE,"E14"),sQuery(id+"F0.wireOp",EDGE,"E15"),sQuery(id+"F0.wireOp",EDGE,"E16"),sQuery(id+"F0.wireOp",EDGE,"E17"),sQuery(id+"F0.wireOp",EDGE,"E18"),sQuery(id+"F0.wireOp",EDGE,"E19"),subQ0,sQuery(id+"F0.wireOp",EDGE,"E21"),sQuery(id+"F0.wireOp",EDGE,"E22"),sQuery(id+"F0.wireOp",EDGE,"E23")])],"isStart":true})]});}
            var Q11;
            {var subQ0=sQuery(id+"F0.wireOp",EDGE,"E21");var subQ1=sQuery(id+"F0.wireOp",EDGE,"E11");Q11=makeQuery(id+"F2.opChamfer","BLEND_EDGE",EDGE,{"blendedFrom":[makeQuery(id+"F1.opExtrude","CAP_EDGE",EDGE,{"disambiguationData":[OSD([subQ1,subQ0])],"isStart":true}),makeQuery(id+"F1.opExtrude","CAP_FACE",FACE,{"disambiguationData":[OSD([sQuery(id+"F0.wireOp",EDGE,"E0"),sQuery(id+"F0.wireOp",EDGE,"E1"),sQuery(id+"F0.wireOp",EDGE,"E8"),sQuery(id+"F0.wireOp",EDGE,"E9"),sQuery(id+"F0.wireOp",EDGE,"E10"),subQ1,sQuery(id+"F0.wireOp",EDGE,"E12"),sQuery(id+"F0.wireOp",EDGE,"E13"),sQuery(id+"F0.wireOp",EDGE,"E14"),sQuery(id+"F0.wireOp",EDGE,"E15"),sQuery(id+"F0.wireOp",EDGE,"E16"),sQuery(id+"F0.wireOp",EDGE,"E17"),sQuery(id+"F0.wireOp",EDGE,"E18"),sQuery(id+"F0.wireOp",EDGE,"E19"),sQuery(id+"F0.wireOp",EDGE,"E20"),subQ0,sQuery(id+"F0.wireOp",EDGE,"E22"),sQuery(id+"F0.wireOp",EDGE,"E23")])],"isStart":true})],"blendedInto":[makeQuery(id+"F1.opExtrude","CAP_FACE",FACE,{"disambiguationData":[OSD([sQuery(id+"F0.wireOp",EDGE,"E0"),sQuery(id+"F0.wireOp",EDGE,"E1"),sQuery(id+"F0.wireOp",EDGE,"E8"),sQuery(id+"F0.wireOp",EDGE,"E9"),sQuery(id+"F0.wireOp",EDGE,"E10"),subQ1,sQuery(id+"F0.wireOp",EDGE,"E12"),sQuery(id+"F0.wireOp",EDGE,"E13"),sQuery(id+"F0.wireOp",EDGE,"E14"),sQuery(id+"F0.wireOp",EDGE,"E15"),sQuery(id+"F0.wireOp",EDGE,"E16"),sQuery(id+"F0.wireOp",EDGE,"E17"),sQuery(id+"F0.wireOp",EDGE,"E18"),sQuery(id+"F0.wireOp",EDGE,"E19"),sQuery(id+"F0.wireOp",EDGE,"E20"),subQ0,sQuery(id+"F0.wireOp",EDGE,"E22"),sQuery(id+"F0.wireOp",EDGE,"E23")])],"isStart":true})]});}
            var Q12;
            {var subQ0=sQuery(id+"F0.wireOp",EDGE,"E22");var subQ1=sQuery(id+"F0.wireOp",EDGE,"E13");Q12=makeQuery(id+"F2.opChamfer","BLEND_EDGE",EDGE,{"blendedFrom":[makeQuery(id+"F1.opExtrude","CAP_EDGE",EDGE,{"disambiguationData":[OSD([subQ1,subQ0])],"isStart":true}),makeQuery(id+"F1.opExtrude","CAP_FACE",FACE,{"disambiguationData":[OSD([sQuery(id+"F0.wireOp",EDGE,"E0"),sQuery(id+"F0.wireOp",EDGE,"E1"),sQuery(id+"F0.wireOp",EDGE,"E8"),sQuery(id+"F0.wireOp",EDGE,"E9"),sQuery(id+"F0.wireOp",EDGE,"E10"),sQuery(id+"F0.wireOp",EDGE,"E11"),sQuery(id+"F0.wireOp",EDGE,"E12"),subQ1,sQuery(id+"F0.wireOp",EDGE,"E14"),sQuery(id+"F0.wireOp",EDGE,"E15"),sQuery(id+"F0.wireOp",EDGE,"E16"),sQuery(id+"F0.wireOp",EDGE,"E17"),sQuery(id+"F0.wireOp",EDGE,"E18"),sQuery(id+"F0.wireOp",EDGE,"E19"),sQuery(id+"F0.wireOp",EDGE,"E20"),sQuery(id+"F0.wireOp",EDGE,"E21"),subQ0,sQuery(id+"F0.wireOp",EDGE,"E23")])],"isStart":true})],"blendedInto":[makeQuery(id+"F1.opExtrude","CAP_FACE",FACE,{"disambiguationData":[OSD([sQuery(id+"F0.wireOp",EDGE,"E0"),sQuery(id+"F0.wireOp",EDGE,"E1"),sQuery(id+"F0.wireOp",EDGE,"E8"),sQuery(id+"F0.wireOp",EDGE,"E9"),sQuery(id+"F0.wireOp",EDGE,"E10"),sQuery(id+"F0.wireOp",EDGE,"E11"),sQuery(id+"F0.wireOp",EDGE,"E12"),subQ1,sQuery(id+"F0.wireOp",EDGE,"E14"),sQuery(id+"F0.wireOp",EDGE,"E15"),sQuery(id+"F0.wireOp",EDGE,"E16"),sQuery(id+"F0.wireOp",EDGE,"E17"),sQuery(id+"F0.wireOp",EDGE,"E18"),sQuery(id+"F0.wireOp",EDGE,"E19"),sQuery(id+"F0.wireOp",EDGE,"E20"),sQuery(id+"F0.wireOp",EDGE,"E21"),subQ0,sQuery(id+"F0.wireOp",EDGE,"E23")])],"isStart":true})]});}
            var Q13;
            {var subQ0=sQuery(id+"F0.wireOp",EDGE,"E23");var subQ1=sQuery(id+"F0.wireOp",EDGE,"E12");Q13=makeQuery(id+"F2.opChamfer","BLEND_EDGE",EDGE,{"blendedFrom":[makeQuery(id+"F1.opExtrude","CAP_EDGE",EDGE,{"disambiguationData":[OSD([subQ1,subQ0])],"isStart":true}),makeQuery(id+"F1.opExtrude","CAP_FACE",FACE,{"disambiguationData":[OSD([sQuery(id+"F0.wireOp",EDGE,"E0"),sQuery(id+"F0.wireOp",EDGE,"E1"),sQuery(id+"F0.wireOp",EDGE,"E8"),sQuery(id+"F0.wireOp",EDGE,"E9"),sQuery(id+"F0.wireOp",EDGE,"E10"),sQuery(id+"F0.wireOp",EDGE,"E11"),subQ1,sQuery(id+"F0.wireOp",EDGE,"E13"),sQuery(id+"F0.wireOp",EDGE,"E14"),sQuery(id+"F0.wireOp",EDGE,"E15"),sQuery(id+"F0.wireOp",EDGE,"E16"),sQuery(id+"F0.wireOp",EDGE,"E17"),sQuery(id+"F0.wireOp",EDGE,"E18"),sQuery(id+"F0.wireOp",EDGE,"E19"),sQuery(id+"F0.wireOp",EDGE,"E20"),sQuery(id+"F0.wireOp",EDGE,"E21"),sQuery(id+"F0.wireOp",EDGE,"E22"),subQ0])],"isStart":true})],"blendedInto":[makeQuery(id+"F1.opExtrude","CAP_FACE",FACE,{"disambiguationData":[OSD([sQuery(id+"F0.wireOp",EDGE,"E0"),sQuery(id+"F0.wireOp",EDGE,"E1"),sQuery(id+"F0.wireOp",EDGE,"E8"),sQuery(id+"F0.wireOp",EDGE,"E9"),sQuery(id+"F0.wireOp",EDGE,"E10"),sQuery(id+"F0.wireOp",EDGE,"E11"),subQ1,sQuery(id+"F0.wireOp",EDGE,"E13"),sQuery(id+"F0.wireOp",EDGE,"E14"),sQuery(id+"F0.wireOp",EDGE,"E15"),sQuery(id+"F0.wireOp",EDGE,"E16"),sQuery(id+"F0.wireOp",EDGE,"E17"),sQuery(id+"F0.wireOp",EDGE,"E18"),sQuery(id+"F0.wireOp",EDGE,"E19"),sQuery(id+"F0.wireOp",EDGE,"E20"),sQuery(id+"F0.wireOp",EDGE,"E21"),sQuery(id+"F0.wireOp",EDGE,"E22"),subQ0])],"isStart":true})]});}
            var Q14;
            {var subQ0=sQuery(id+"F0.wireOp",EDGE,"E16");var subQ1=sQuery(id+"F0.wireOp",EDGE,"E14");Q14=makeQuery(id+"F2.opChamfer","BLEND_EDGE",EDGE,{"blendedFrom":[makeQuery(id+"F1.opExtrude","CAP_EDGE",EDGE,{"disambiguationData":[OSD([subQ1,subQ0])],"isStart":true}),makeQuery(id+"F1.opExtrude","CAP_FACE",FACE,{"disambiguationData":[OSD([sQuery(id+"F0.wireOp",EDGE,"E0"),sQuery(id+"F0.wireOp",EDGE,"E1"),sQuery(id+"F0.wireOp",EDGE,"E8"),sQuery(id+"F0.wireOp",EDGE,"E9"),sQuery(id+"F0.wireOp",EDGE,"E10"),sQuery(id+"F0.wireOp",EDGE,"E11"),sQuery(id+"F0.wireOp",EDGE,"E12"),sQuery(id+"F0.wireOp",EDGE,"E13"),subQ1,sQuery(id+"F0.wireOp",EDGE,"E15"),subQ0,sQuery(id+"F0.wireOp",EDGE,"E17"),sQuery(id+"F0.wireOp",EDGE,"E18"),sQuery(id+"F0.wireOp",EDGE,"E19"),sQuery(id+"F0.wireOp",EDGE,"E20"),sQuery(id+"F0.wireOp",EDGE,"E21"),sQuery(id+"F0.wireOp",EDGE,"E22"),sQuery(id+"F0.wireOp",EDGE,"E23")])],"isStart":true})],"blendedInto":[makeQuery(id+"F1.opExtrude","CAP_FACE",FACE,{"disambiguationData":[OSD([sQuery(id+"F0.wireOp",EDGE,"E0"),sQuery(id+"F0.wireOp",EDGE,"E1"),sQuery(id+"F0.wireOp",EDGE,"E8"),sQuery(id+"F0.wireOp",EDGE,"E9"),sQuery(id+"F0.wireOp",EDGE,"E10"),sQuery(id+"F0.wireOp",EDGE,"E11"),sQuery(id+"F0.wireOp",EDGE,"E12"),sQuery(id+"F0.wireOp",EDGE,"E13"),subQ1,sQuery(id+"F0.wireOp",EDGE,"E15"),subQ0,sQuery(id+"F0.wireOp",EDGE,"E17"),sQuery(id+"F0.wireOp",EDGE,"E18"),sQuery(id+"F0.wireOp",EDGE,"E19"),sQuery(id+"F0.wireOp",EDGE,"E20"),sQuery(id+"F0.wireOp",EDGE,"E21"),sQuery(id+"F0.wireOp",EDGE,"E22"),sQuery(id+"F0.wireOp",EDGE,"E23")])],"isStart":true})]});}
            var Q15;
            {var subQ0=sQuery(id+"F0.wireOp",EDGE,"E17");var subQ1=sQuery(id+"F0.wireOp",EDGE,"E15");Q15=makeQuery(id+"F2.opChamfer","BLEND_EDGE",EDGE,{"blendedFrom":[makeQuery(id+"F1.opExtrude","CAP_EDGE",EDGE,{"disambiguationData":[OSD([subQ1,subQ0])],"isStart":true}),makeQuery(id+"F1.opExtrude","CAP_FACE",FACE,{"disambiguationData":[OSD([sQuery(id+"F0.wireOp",EDGE,"E0"),sQuery(id+"F0.wireOp",EDGE,"E1"),sQuery(id+"F0.wireOp",EDGE,"E8"),sQuery(id+"F0.wireOp",EDGE,"E9"),sQuery(id+"F0.wireOp",EDGE,"E10"),sQuery(id+"F0.wireOp",EDGE,"E11"),sQuery(id+"F0.wireOp",EDGE,"E12"),sQuery(id+"F0.wireOp",EDGE,"E13"),sQuery(id+"F0.wireOp",EDGE,"E14"),subQ1,sQuery(id+"F0.wireOp",EDGE,"E16"),subQ0,sQuery(id+"F0.wireOp",EDGE,"E18"),sQuery(id+"F0.wireOp",EDGE,"E19"),sQuery(id+"F0.wireOp",EDGE,"E20"),sQuery(id+"F0.wireOp",EDGE,"E21"),sQuery(id+"F0.wireOp",EDGE,"E22"),sQuery(id+"F0.wireOp",EDGE,"E23")])],"isStart":true})],"blendedInto":[makeQuery(id+"F1.opExtrude","CAP_FACE",FACE,{"disambiguationData":[OSD([sQuery(id+"F0.wireOp",EDGE,"E0"),sQuery(id+"F0.wireOp",EDGE,"E1"),sQuery(id+"F0.wireOp",EDGE,"E8"),sQuery(id+"F0.wireOp",EDGE,"E9"),sQuery(id+"F0.wireOp",EDGE,"E10"),sQuery(id+"F0.wireOp",EDGE,"E11"),sQuery(id+"F0.wireOp",EDGE,"E12"),sQuery(id+"F0.wireOp",EDGE,"E13"),sQuery(id+"F0.wireOp",EDGE,"E14"),subQ1,sQuery(id+"F0.wireOp",EDGE,"E16"),subQ0,sQuery(id+"F0.wireOp",EDGE,"E18"),sQuery(id+"F0.wireOp",EDGE,"E19"),sQuery(id+"F0.wireOp",EDGE,"E20"),sQuery(id+"F0.wireOp",EDGE,"E21"),sQuery(id+"F0.wireOp",EDGE,"E22"),sQuery(id+"F0.wireOp",EDGE,"E23")])],"isStart":true})]});}
            chamfer(context, id + "F3", {"entities" : qUnion([Q0, Q1, Q2, Q3, Q4, Q5, Q6, Q7, Q8, Q9, Q10, Q11, Q12, Q13, Q14, Q15]), "width" : 81.28 * mm, "tangentPropagation" : true});
        }
        {
            var Q0;
            {var subQ0=sQuery(id+"F0.wireOp",EDGE,"E1");Q0=makeQuery(id+"F1.opExtrude","CAP_EDGE",EDGE,{"disambiguationData":[OSD([subQ0]),TDD([makeQuery(id+"F0.imprint","IMPRINT",EDGE,{"disambiguationData":[TD([[makeQuery(id+"F0.imprint","INTERSECT",VERTEX,{"derivedFrom":[subQ0,sQuery(id+"F0.wireOp",EDGE,"E16")]}),1.0]])],"derivedFrom":subQ0})])],"isStart":true});}
            var Q1;
            {var subQ0=sQuery(id+"F0.wireOp",EDGE,"E1");Q1=makeQuery(id+"F1.opExtrude","CAP_EDGE",EDGE,{"disambiguationData":[OSD([subQ0]),TDD([makeQuery(id+"F0.imprint","IMPRINT",EDGE,{"disambiguationData":[TD([[makeQuery(id+"F0.imprint","INTERSECT",VERTEX,{"derivedFrom":[subQ0,sQuery(id+"F0.wireOp",EDGE,"E16")]}),1.0]])],"derivedFrom":subQ0})])],"isStart":false});}
            var Q2;
            {var subQ0=sQuery(id+"F0.wireOp",EDGE,"E1");Q2=makeQuery(id+"F1.opExtrude","CAP_EDGE",EDGE,{"disambiguationData":[OSD([subQ0]),TDD([makeQuery(id+"F0.imprint","IMPRINT",EDGE,{"disambiguationData":[TD([[makeQuery(id+"F0.imprint","INTERSECT",VERTEX,{"derivedFrom":[subQ0,sQuery(id+"F0.wireOp",EDGE,"E19")]}),1.0]])],"derivedFrom":subQ0})])],"isStart":true});}
            var Q3;
            {var subQ0=sQuery(id+"F0.wireOp",EDGE,"E1");Q3=makeQuery(id+"F1.opExtrude","CAP_EDGE",EDGE,{"disambiguationData":[OSD([subQ0]),TDD([makeQuery(id+"F0.imprint","IMPRINT",EDGE,{"disambiguationData":[TD([[makeQuery(id+"F0.imprint","INTERSECT",VERTEX,{"derivedFrom":[subQ0,sQuery(id+"F0.wireOp",EDGE,"E19")]}),1.0]])],"derivedFrom":subQ0})])],"isStart":false});}
            var Q4;
            {var subQ0=sQuery(id+"F0.wireOp",EDGE,"E1");Q4=makeQuery(id+"F1.opExtrude","CAP_EDGE",EDGE,{"disambiguationData":[OSD([subQ0]),TDD([makeQuery(id+"F0.imprint","IMPRINT",EDGE,{"disambiguationData":[TD([[makeQuery(id+"F0.imprint","INTERSECT",VERTEX,{"derivedFrom":[subQ0,sQuery(id+"F0.wireOp",EDGE,"E21")]}),1.0]])],"derivedFrom":subQ0})])],"isStart":true});}
            var Q5;
            {var subQ0=sQuery(id+"F0.wireOp",EDGE,"E1");Q5=makeQuery(id+"F1.opExtrude","CAP_EDGE",EDGE,{"disambiguationData":[OSD([subQ0]),TDD([makeQuery(id+"F0.imprint","IMPRINT",EDGE,{"disambiguationData":[TD([[makeQuery(id+"F0.imprint","INTERSECT",VERTEX,{"derivedFrom":[subQ0,sQuery(id+"F0.wireOp",EDGE,"E21")]}),1.0]])],"derivedFrom":subQ0})])],"isStart":false});}
            var Q6;
            {var subQ0=sQuery(id+"F0.wireOp",EDGE,"E1");Q6=makeQuery(id+"F1.opExtrude","CAP_EDGE",EDGE,{"disambiguationData":[OSD([subQ0]),TDD([makeQuery(id+"F0.imprint","IMPRINT",EDGE,{"disambiguationData":[TD([[makeQuery(id+"F0.imprint","INTERSECT",VERTEX,{"derivedFrom":[subQ0,sQuery(id+"F0.wireOp",EDGE,"E17")]}),-1.0]])],"derivedFrom":subQ0})])],"isStart":true});}
            var Q7;
            {var subQ0=sQuery(id+"F0.wireOp",EDGE,"E1");Q7=makeQuery(id+"F1.opExtrude","CAP_EDGE",EDGE,{"disambiguationData":[OSD([subQ0]),TDD([makeQuery(id+"F0.imprint","IMPRINT",EDGE,{"disambiguationData":[TD([[makeQuery(id+"F0.imprint","INTERSECT",VERTEX,{"derivedFrom":[subQ0,sQuery(id+"F0.wireOp",EDGE,"E17")]}),-1.0]])],"derivedFrom":subQ0})])],"isStart":false});}
            fillet(context, id + "F4", {"entities" : qUnion([Q0, Q1, Q2, Q3, Q4, Q5, Q6, Q7]), "radius" : 50.8 * mm, "tangentPropagation" : true, "allowEdgeOverflow" : false});
        }
    });
